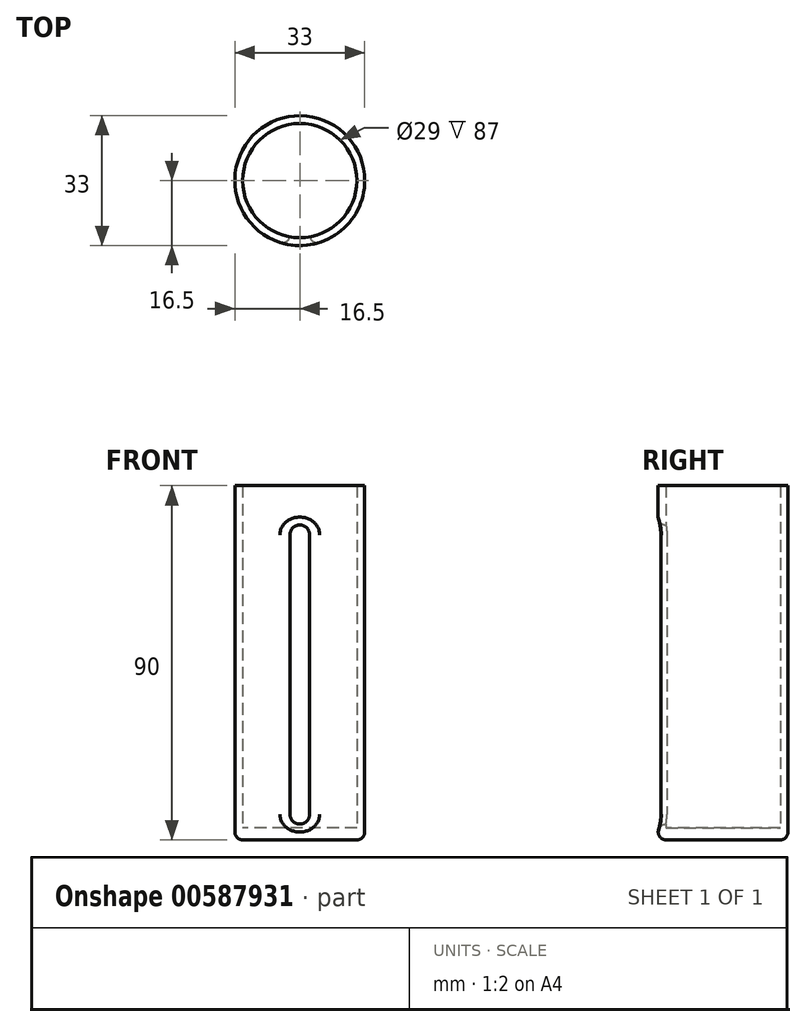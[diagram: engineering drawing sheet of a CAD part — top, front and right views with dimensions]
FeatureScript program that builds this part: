
annotation { "Feature Type Name" : "Feature", "Feature Type Description" : "" }
export const myFeature = defineFeature(function(context is Context, id is Id, definition is map)
    precondition{}
    {
        {
            var Q0;
            Q0=qCreatedBy(makeId("Top.planeOp"),FACE);
            var sketch = newSketch(context, id + "F0", { "sketchPlane" : qUnion([Q0])});
            skCircle(sketch, "E0", {"center": v(0, 0) * mm, "radius": 14.5 * mm});
            skCircle(sketch, "E1.0", {"center": v(0, 0) * mm, "radius": 16.5 * mm});
            skSolve(sketch);
        }
        {
            var Q0;
            Q0=makeQuery(id+"F0.imprint","IMPRINT",FACE,{"disambiguationData":[TD([[makeQuery(id+"F0.imprint","IMPRINT",EDGE,{"derivedFrom":sQuery(id+"F0.wireOp",EDGE,"E0")}),-1.0]])]});
            extrude(context, id + "F1", {"entities" : qUnion([Q0]), "depth" : 90 * mm, "offsetDistance" : 25 * mm});
        }
        {
            var Q0;
            Q0=makeQuery(id+"F0.imprint","IMPRINT",FACE,{"disambiguationData":[TD([[makeQuery(id+"F0.imprint","IMPRINT",EDGE,{"derivedFrom":sQuery(id+"F0.wireOp",EDGE,"E0")}),1.0]])]});
            extrude(context, id + "F2", {"entities" : qUnion([Q0]), "operationType" : NewBodyOperationType.ADD, "depth" : 3 * mm, "offsetDistance" : 25 * mm});
        }
        {
            var Q0;
            Q0=qCreatedBy(makeId("Front.planeOp"),FACE);
            var sketch = newSketch(context, id + "F3", { "sketchPlane" : qUnion([Q0])});
            skLineSegment(sketch, "E2.bottom", {"start": v(0, 80) * mm, "end": v(0, 80) * mm});
            skLineSegment(sketch, "E2.top", {"start": v(0, 4) * mm, "end": v(0, 4) * mm});
            skLineSegment(sketch, "E2.left", {"start": v(-2.5, 77.5) * mm, "end": v(-2.5, 6.5) * mm});
            skLineSegment(sketch, "E2.right", {"start": v(2.5, 77.5) * mm, "end": v(2.5, 6.5) * mm});
            skPoint(sketch, "E3.visualSharp", {"position": v(-2.5, 80) * mm});
            skArc(sketch, "E3.filletArc", {"start": v(0, 80) * mm, "mid": v(-1.77, 79.27) * mm, "end": v(-2.5, 77.5) * mm});
            skPoint(sketch, "E4.visualSharp", {"position": v(2.5, 4) * mm});
            skArc(sketch, "E4.filletArc", {"start": v(0, 4) * mm, "mid": v(1.77, 4.73) * mm, "end": v(2.5, 6.5) * mm});
            skPoint(sketch, "E5.visualSharp", {"position": v(2.5, 80) * mm});
            skArc(sketch, "E5.filletArc", {"start": v(2.5, 77.5) * mm, "mid": v(1.77, 79.27) * mm, "end": v(0, 80) * mm});
            skPoint(sketch, "E6.visualSharp", {"position": v(-2.5, 4) * mm});
            skArc(sketch, "E6.filletArc", {"start": v(-2.5, 6.5) * mm, "mid": v(-1.77, 4.73) * mm, "end": v(0, 4) * mm});
            skSolve(sketch);
        }
        {
            var Q0;
            Q0 = qSketchRegion(id + "F3", true);
            extrude(context, id + "F4", {"entities" : qUnion([Q0]), "operationType" : NewBodyOperationType.REMOVE, "depth" : 25 * mm, "offsetDistance" : 25 * mm});
        }
        {
            var Q0;
            Q0=makeQuery(id+"F4.boolean.opBoolean","INTERSECT",EDGE,{"derivedFrom":[makeQuery(id+"F1.opExtrude","SWEPT_FACE",FACE,{"disambiguationData":[OSD([sQuery(id+"F0.wireOp",EDGE,"E1.0")])]}),makeQuery(id+"F4.opExtrude","SWEPT_FACE",FACE,{"disambiguationData":[OSD([sQuery(id+"F3.wireOp",EDGE,"E2.right")])]})]});
            var Q1;
            Q1=makeQuery(id+"F1.opExtrude","CAP_EDGE",EDGE,{"disambiguationData":[OSD([sQuery(id+"F0.wireOp",EDGE,"E1.0")])],"isStart":true});
            fillet(context, id + "F5", {"entities" : qUnion([Q0, Q1]), "radius" : 2 * mm, "tangentPropagation" : true, "allowEdgeOverflow" : false});
        }
    });
